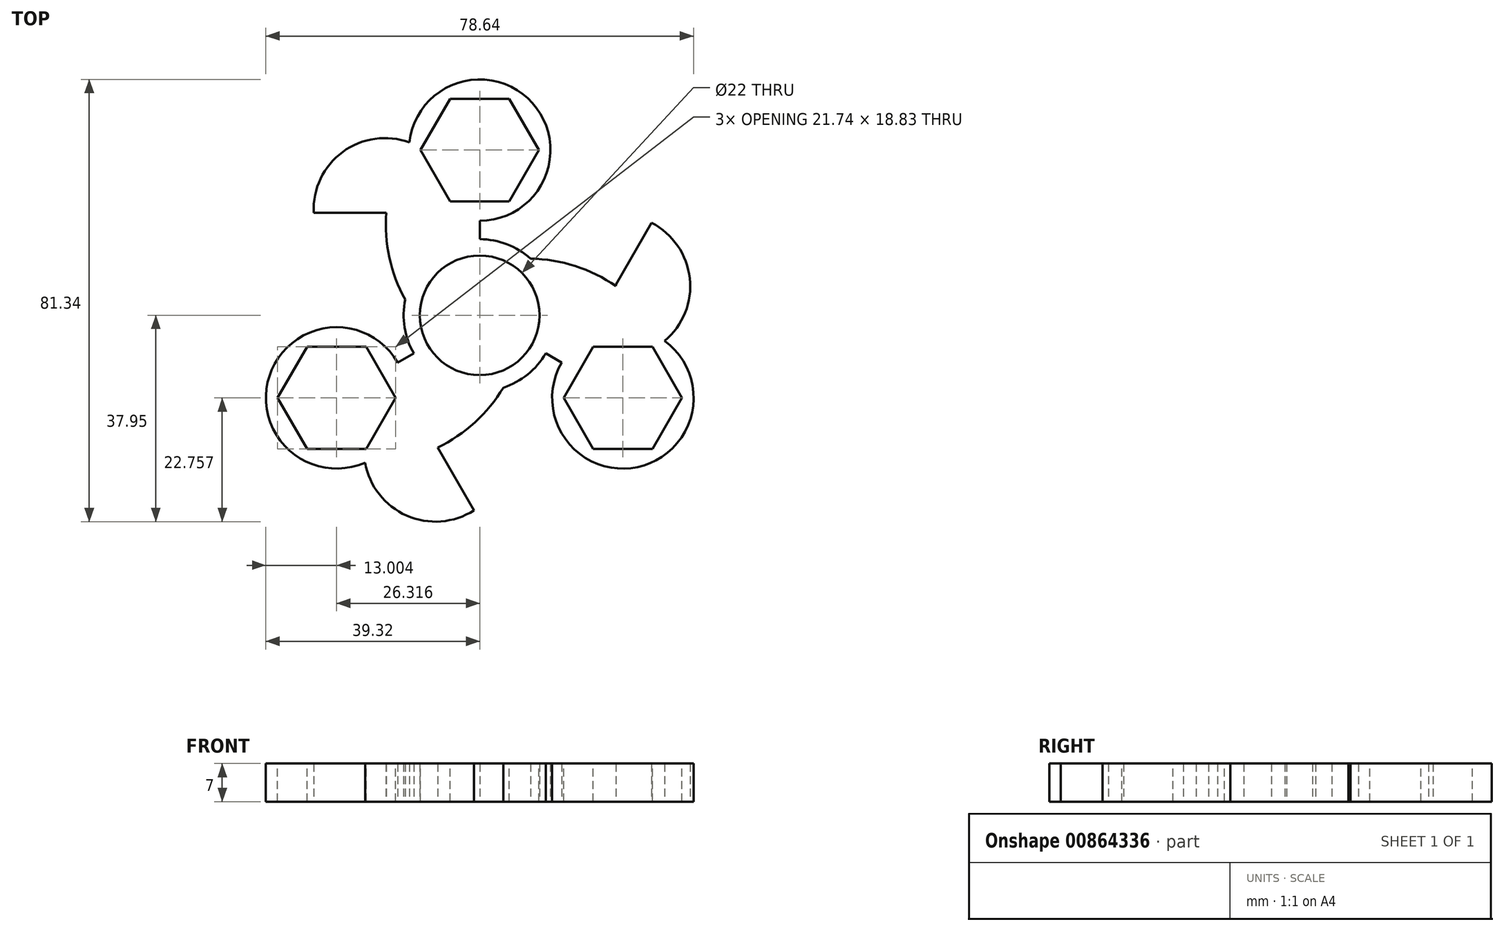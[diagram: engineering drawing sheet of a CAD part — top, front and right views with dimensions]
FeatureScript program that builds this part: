
annotation { "Feature Type Name" : "Feature", "Feature Type Description" : "" }
export const myFeature = defineFeature(function(context is Context, id is Id, definition is map)
    precondition{}
    {
        {
            var Q0;
            Q0=qCreatedBy(makeId("Top.planeOp"),FACE);
            var sketch = newSketch(context, id + "F0", { "sketchPlane" : qUnion([Q0])});
            skCircle(sketch, "E0", {"center": v(0, 0) * mm, "radius": 11 * mm});
            skArc(sketch, "E1.0", {"start": v(4.35, -13.3) * mm, "mid": v(8.82, -10.87) * mm, "end": v(12.12, -7) * mm});
            skCircle(sketch, "E2", {"center": v(0, 0) * mm, "radius": 43.39 * mm, "construction": true});
            skArc(sketch, "E3", {"start": v(0, 17.39) * mm, "mid": v(9.68, 39.07) * mm, "end": v(-12.92, 31.79) * mm});
            skArc(sketch, "E4", {"start": v(-17.2, 18.87) * mm, "mid": v(-16.62, 10.62) * mm, "end": v(-13.7, 2.89) * mm});
            skLineSegment(sketch, "E5", {"start": v(0, 17.39) * mm, "end": v(0, 14) * mm});
            skArc(sketch, "E6", {"start": v(-12.92, 31.79) * mm, "mid": v(-25.2, 30.05) * mm, "end": v(-30.53, 18.87) * mm});
            skLineSegment(sketch, "E7", {"start": v(-30.53, 18.87) * mm, "end": v(-17.44, 18.87) * mm});
            skLineSegment(sketch, "E8", {"start": v(-17.44, 18.87) * mm, "end": v(-17.2, 18.87) * mm});
            skArc(sketch, "E9.1.0", {"start": v(-15.06, -8.7) * mm, "mid": v(-38.67, -11.16) * mm, "end": v(-21.07, -27.09) * mm});
            skArc(sketch, "E9.1.1", {"start": v(-21.07, -27.09) * mm, "mid": v(-13.43, -36.85) * mm, "end": v(-1.08, -35.87) * mm});
            skLineSegment(sketch, "E9.1.2", {"start": v(-1.08, -35.87) * mm, "end": v(-7.62, -24.54) * mm});
            skArc(sketch, "E9.1.3", {"start": v(-7.75, -24.32) * mm, "mid": v(-0.89, -19.7) * mm, "end": v(4.35, -13.3) * mm});
            skLineSegment(sketch, "E9.1.4", {"start": v(-15.06, -8.7) * mm, "end": v(-12.12, -7) * mm});
            skArc(sketch, "E9.2.0", {"start": v(15.06, -8.7) * mm, "mid": v(29, -27.91) * mm, "end": v(34, -4.7) * mm});
            skArc(sketch, "E9.2.1", {"start": v(34, -4.7) * mm, "mid": v(38.63, 6.8) * mm, "end": v(31.6, 17) * mm});
            skLineSegment(sketch, "E9.2.2", {"start": v(31.6, 17) * mm, "end": v(25.06, 5.67) * mm});
            skArc(sketch, "E9.2.3", {"start": v(25.06, 5.37) * mm, "mid": v(17.58, 9.06) * mm, "end": v(9.35, 10.42) * mm});
            skLineSegment(sketch, "E9.2.4", {"start": v(15.06, -8.7) * mm, "end": v(12.12, -7) * mm});
            skLineSegment(sketch, "E10", {"start": v(-7.62, -24.54) * mm, "end": v(-7.75, -24.32) * mm});
            skLineSegment(sketch, "E11", {"start": v(25.06, 5.67) * mm, "end": v(25.06, 5.37) * mm});
            skArc(sketch, "E12.trimOffspring", {"start": v(-13.7, 2.89) * mm, "mid": v(-13.83, -2.2) * mm, "end": v(-12.12, -7) * mm});
            skArc(sketch, "E13.trimOffspring", {"start": v(9.35, 10.42) * mm, "mid": v(5, 13.07) * mm, "end": v(0, 14) * mm});
            skSolve(sketch);
        }
        {
            var Q0;
            Q0=makeQuery(id+"F0.imprint","IMPRINT",FACE,{"disambiguationData":[TD([[makeQuery(id+"F0.imprint","IMPRINT",EDGE,{"derivedFrom":sQuery(id+"F0.wireOp",EDGE,"E0")}),-1.0]])]});
            extrude(context, id + "F1", {"entities" : qUnion([Q0]), "depth" : 7 * mm, "offsetDistance" : 25 * mm});
        }
        {
            var Q0;
            Q0=makeQuery(id+"F1.opExtrude","CAP_FACE",FACE,{"disambiguationData":[OSD([sQuery(id+"F0.wireOp",EDGE,"E0"),sQuery(id+"F0.wireOp",EDGE,"E1.0"),sQuery(id+"F0.wireOp",EDGE,"E3"),sQuery(id+"F0.wireOp",EDGE,"E4"),sQuery(id+"F0.wireOp",EDGE,"E5"),sQuery(id+"F0.wireOp",EDGE,"E6"),sQuery(id+"F0.wireOp",EDGE,"E7"),sQuery(id+"F0.wireOp",EDGE,"E8"),sQuery(id+"F0.wireOp",EDGE,"E9.1.0"),sQuery(id+"F0.wireOp",EDGE,"E9.1.1"),sQuery(id+"F0.wireOp",EDGE,"E9.1.2"),sQuery(id+"F0.wireOp",EDGE,"E9.1.3"),sQuery(id+"F0.wireOp",EDGE,"E9.1.4"),sQuery(id+"F0.wireOp",EDGE,"E9.2.0"),sQuery(id+"F0.wireOp",EDGE,"E9.2.1"),sQuery(id+"F0.wireOp",EDGE,"E9.2.2"),sQuery(id+"F0.wireOp",EDGE,"E9.2.3"),sQuery(id+"F0.wireOp",EDGE,"E9.2.4"),sQuery(id+"F0.wireOp",EDGE,"E10"),sQuery(id+"F0.wireOp",EDGE,"E11"),sQuery(id+"F0.wireOp",EDGE,"E12.trimOffspring"),sQuery(id+"F0.wireOp",EDGE,"E13.trimOffspring")])],"isStart":false});
            var sketch = newSketch(context, id + "F2", { "sketchPlane" : qUnion([Q0])});
            skCircle(sketch, "E14.cCircle", {"center": v(0, 30.39) * mm, "radius": 9.41 * mm, "construction": true});
            skLineSegment(sketch, "E14.0", {"start": v(-5.44, 39.8) * mm, "end": v(5.44, 39.8) * mm});
            skLineSegment(sketch, "E14.1", {"start": v(5.44, 39.8) * mm, "end": v(10.87, 30.39) * mm});
            skLineSegment(sketch, "E14.2", {"start": v(10.87, 30.39) * mm, "end": v(5.44, 20.97) * mm});
            skLineSegment(sketch, "E14.3", {"start": v(5.44, 20.97) * mm, "end": v(-5.44, 20.97) * mm});
            skLineSegment(sketch, "E14.4", {"start": v(-5.44, 20.97) * mm, "end": v(-10.87, 30.39) * mm});
            skLineSegment(sketch, "E14.5", {"start": v(-10.87, 30.39) * mm, "end": v(-5.44, 39.8) * mm});
            skPoint(sketch, "E14.0.midPoint", {"position": v(0, 39.8) * mm});
            skLineSegment(sketch, "E15.1.0", {"start": v(-31.75, -24.6) * mm, "end": v(-37.19, -15.2) * mm});
            skLineSegment(sketch, "E15.1.1", {"start": v(-20.88, -5.78) * mm, "end": v(-15.44, -15.2) * mm});
            skLineSegment(sketch, "E15.1.2", {"start": v(-31.75, -5.78) * mm, "end": v(-20.88, -5.78) * mm});
            skLineSegment(sketch, "E15.1.3", {"start": v(-37.19, -15.2) * mm, "end": v(-31.75, -5.78) * mm});
            skLineSegment(sketch, "E15.1.4", {"start": v(-20.88, -24.6) * mm, "end": v(-31.75, -24.6) * mm});
            skLineSegment(sketch, "E15.1.5", {"start": v(-15.44, -15.2) * mm, "end": v(-20.88, -24.6) * mm});
            skCircle(sketch, "E15.1.6", {"center": v(-26.32, -15.2) * mm, "radius": 9.41 * mm, "construction": true});
            skLineSegment(sketch, "E15.2.0", {"start": v(37.19, -15.2) * mm, "end": v(31.75, -24.6) * mm});
            skLineSegment(sketch, "E15.2.1", {"start": v(15.44, -15.2) * mm, "end": v(20.88, -5.78) * mm});
            skLineSegment(sketch, "E15.2.2", {"start": v(20.88, -24.6) * mm, "end": v(15.44, -15.2) * mm});
            skLineSegment(sketch, "E15.2.3", {"start": v(31.75, -24.6) * mm, "end": v(20.88, -24.6) * mm});
            skLineSegment(sketch, "E15.2.4", {"start": v(31.75, -5.78) * mm, "end": v(37.19, -15.2) * mm});
            skLineSegment(sketch, "E15.2.5", {"start": v(20.88, -5.78) * mm, "end": v(31.75, -5.78) * mm});
            skCircle(sketch, "E15.2.6", {"center": v(26.32, -15.2) * mm, "radius": 9.41 * mm, "construction": true});
            skPoint(sketch, "E15.center", {"position": v(0, 0) * mm});
            skSolve(sketch);
        }
        {
            var Q0;
            Q0=makeQuery(id+"F2.imprint","IMPRINT",FACE,{"disambiguationData":[TD([[makeQuery(id+"F2.imprint","IMPRINT",EDGE,{"derivedFrom":sQuery(id+"F2.wireOp",EDGE,"E14.0")}),-1.0]])]});
            var Q1;
            Q1=makeQuery(id+"F2.imprint","IMPRINT",FACE,{"disambiguationData":[TD([[makeQuery(id+"F2.imprint","IMPRINT",EDGE,{"derivedFrom":sQuery(id+"F2.wireOp",EDGE,"E15.1.0")}),-1.0]])]});
            var Q2;
            Q2=makeQuery(id+"F2.imprint","IMPRINT",FACE,{"disambiguationData":[TD([[makeQuery(id+"F2.imprint","IMPRINT",EDGE,{"derivedFrom":sQuery(id+"F2.wireOp",EDGE,"E15.2.0")}),-1.0]])]});
            extrude(context, id + "F3", {"entities" : qUnion([Q0, Q1, Q2]), "operationType" : NewBodyOperationType.REMOVE, "oppositeDirection" : true, "depth" : 25 * mm, "offsetDistance" : 25 * mm});
        }
    });
